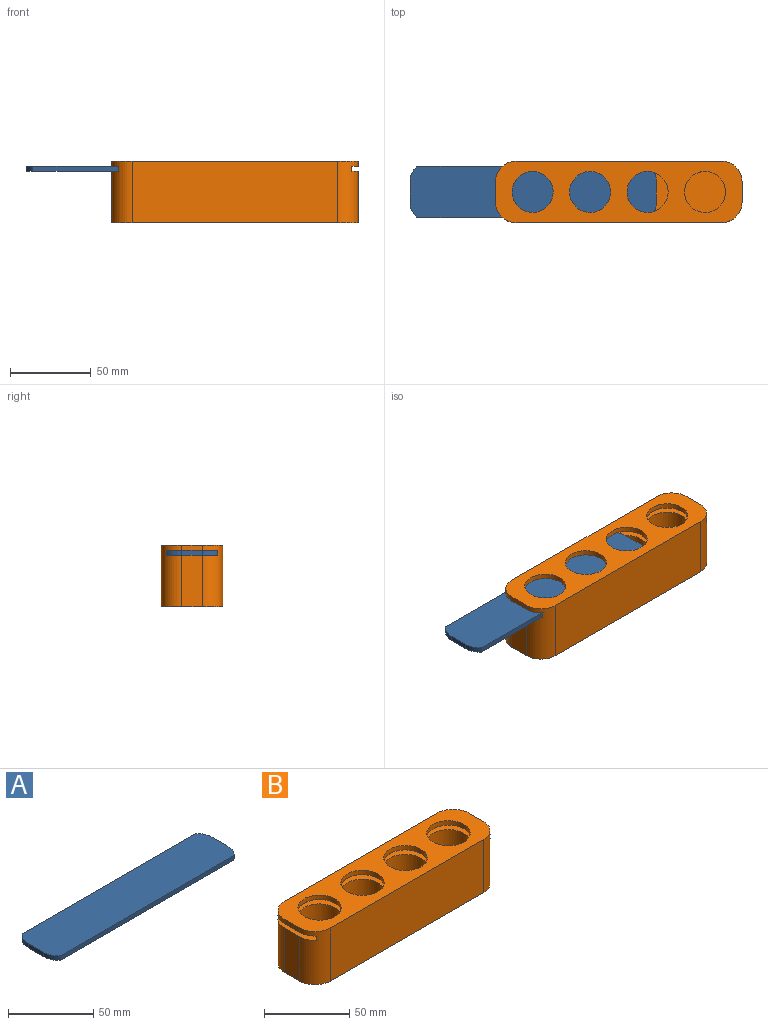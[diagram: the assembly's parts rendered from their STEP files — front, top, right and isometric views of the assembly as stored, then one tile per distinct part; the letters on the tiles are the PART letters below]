
ASSEMBLY  parts=2 mates=1
PART A: 10 faces, bbox 152.4x31.8x3.2 mm
  f0: plane 143.8x3.18mm, normal (0,-1,0), area 456.6mm2, adj f1,f7,f8,f9
  f1: cylinder r=12.7mm len=9.53mm, axis (0,0,-1), area 34.2mm2, adj f0,f2,f8,f9
  f2: plane 12.7x3.18mm, normal (1,0,0), area 40.3mm2, adj f1,f3,f8,f9
  f3: cylinder r=12.7mm len=9.53mm, axis (0,0,-1), area 34.2mm2, adj f2,f4,f8,f9
  f4: plane 143.8x3.18mm, normal (0,1,0), area 456.6mm2, adj f3,f5,f8,f9
  f5: cylinder r=12.7mm len=9.53mm, axis (0,0,-1), area 34.2mm2, adj f4,f6,f8,f9
  f6: plane 12.7x3.18mm, normal (-1,0,0), area 40.3mm2, adj f5,f7,f8,f9
  f7: cylinder r=12.7mm len=9.53mm, axis (0,0,-1), area 34.2mm2, adj f0,f6,f8,f9
  f8: plane 152.4x31.75mm, normal (0,0,1), area 4788.4mm2, adj f0,f1,f2,f3,f4,f5,f6,f7
  f9: plane 152.4x31.75mm, normal (0,0,-1), area 4788.4mm2, adj f0,f1,f2,f3,f4,f5,f6,f7
PART B: 28 faces, bbox 152.4x38.1x38.1 mm
  f0: plane 12.7x3.18mm, normal (-1,0,0), area 40.3mm2, adj f1,f5,f6,f19
  f1: cylinder r=12.7mm len=38.1mm, axis (0,0,-1), area 725.9mm2, adj f0,f6,f7,f8,f11,f16,f18,f19
  f2: cylinder r=12.7mm len=38.1mm, axis (0,0,-1), area 725.9mm2, adj f3,f6,f8,f9,f11,f16,f18,f19
  f3: plane 31.75x12.7mm, normal (1,0,0), area 403.2mm2, adj f2,f4,f11,f18
  f4: cylinder r=12.7mm len=38.1mm, axis (0,0,-1), area 725.9mm2, adj f3,f6,f9,f10,f11,f17,f18,f19
  f5: cylinder r=12.7mm len=38.1mm, axis (0,0,-1), area 725.9mm2, adj f0,f6,f7,f10,f11,f17,f18,f19
  f6: plane 152.4x38.1mm, normal (0,0,1), area 3641.2mm2, adj f0,f1,f2,f4,f5,f8,f9,f10
  f7: plane 31.75x12.7mm, normal (-1,0,0), area 403.2mm2, adj f1,f5,f11,f18
  f8: plane 127x38.1mm, normal (0,-1,0), area 4838.7mm2, adj f1,f2,f6,f11
  f9: plane 12.7x3.18mm, normal (1,0,0), area 40.3mm2, adj f2,f4,f6,f19
  f10: plane 127x38.1mm, normal (0,1,0), area 4838.7mm2, adj f4,f5,f6,f11
  f11: plane 152.4x38.1mm, normal (0,0,-1), area 5668mm2, adj f1,f2,f3,f4,f5,f7,f8,f10
  f12: cylinder r=12.7mm len=25.4mm, axis (0,0,1), area 253.4mm2, adj f6,f19
  f13: cylinder r=12.7mm len=25.4mm, axis (0,0,1), area 253.4mm2, adj f6,f19
  f14: cylinder r=12.7mm len=25.4mm, axis (0,0,1), area 253.4mm2, adj f6,f19
  f15: cylinder r=12.7mm len=25.4mm, axis (0,0,1), area 253.4mm2, adj f6,f19
  f16: plane 143.8x3.18mm, normal (0,1,0), area 456.6mm2, adj f1,f2,f18,f19
  f17: plane 143.8x3.18mm, normal (0,-1,0), area 456.6mm2, adj f4,f5,f18,f19
  f18: plane 152.4x31.75mm, normal (0,0,1), area 2761.6mm2, adj f1,f2,f3,f4,f5,f7,f16,f17
  f19: plane 152.4x31.75mm, normal (0,0,-1), area 2761.6mm2, adj f0,f1,f2,f4,f5,f9,f12,f13
  f20: plane 25.4x25.4mm, normal (0,0,1), area 506.7mm2, adj f21
  f21: cylinder r=12.7mm len=25.4mm, axis (0,0,1), area 2026.8mm2, adj f18,f20
  f22: plane 25.4x25.4mm, normal (0,0,1), area 506.7mm2, adj f23
  f23: cylinder r=12.7mm len=25.4mm, axis (0,0,1), area 2026.8mm2, adj f18,f22
  f24: plane 25.4x25.4mm, normal (0,0,1), area 506.7mm2, adj f25
  f25: cylinder r=12.7mm len=25.4mm, axis (0,0,1), area 2026.8mm2, adj f18,f24
  f26: plane 25.4x25.4mm, normal (0,0,1), area 506.7mm2, adj f27
  f27: cylinder r=12.7mm len=25.4mm, axis (0,0,1), area 2026.8mm2, adj f18,f26
PLACE A rot(axis=(1,0,0),0deg) t=(75.41,89.69,23.05)mm
PLACE B rot(axis=(1,0,0),0deg) t=(133.74,40.84,-8.7)mm
MATE parallel A.f9 <-> B.f18  axis (0,0,-1) through (8.88,24.97,23.05)mm
